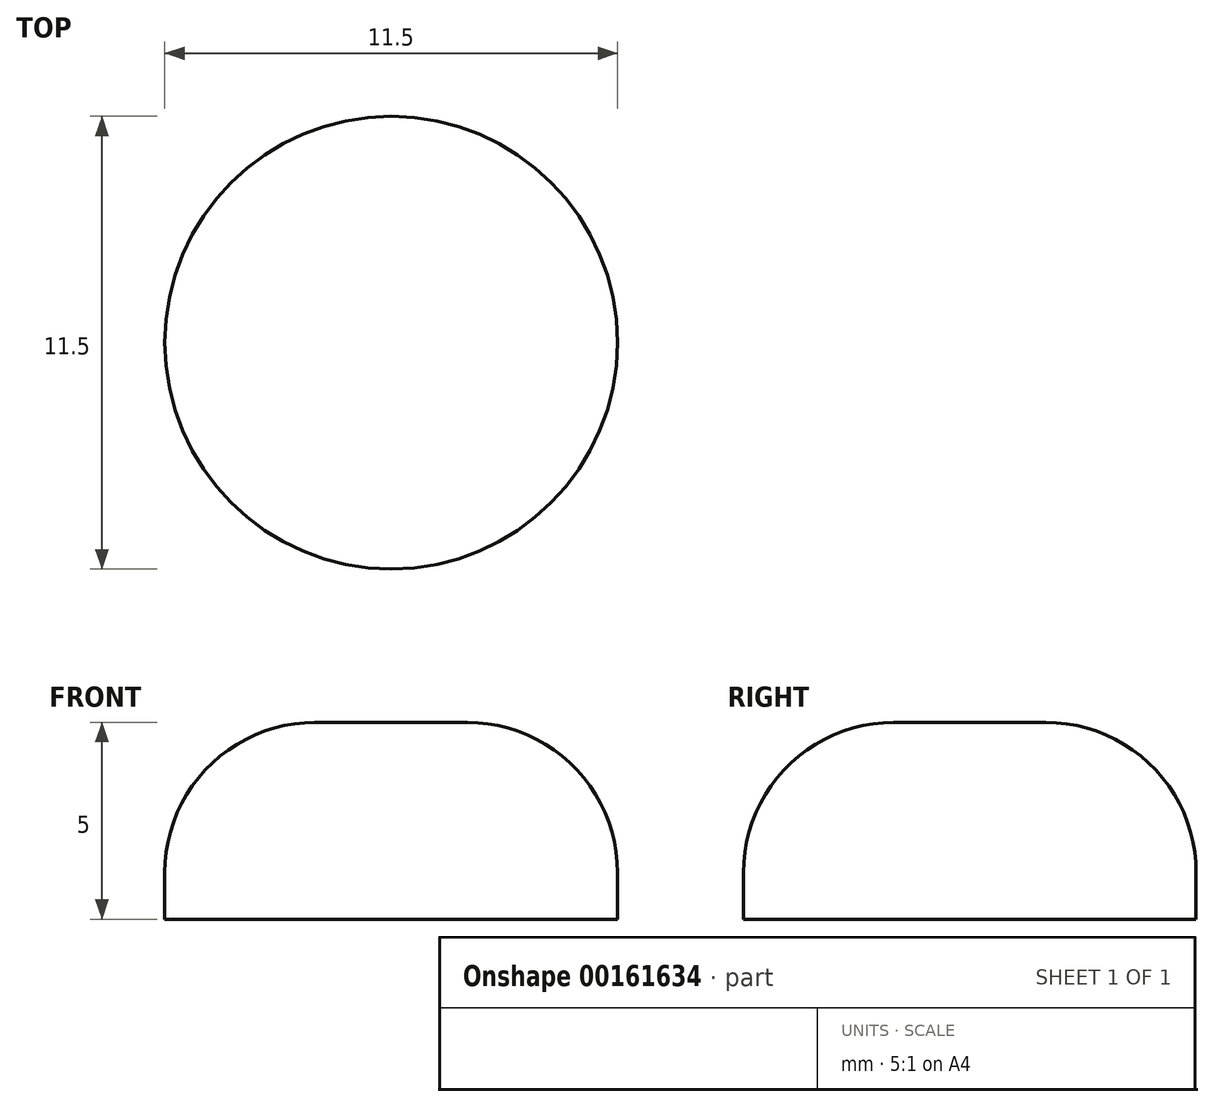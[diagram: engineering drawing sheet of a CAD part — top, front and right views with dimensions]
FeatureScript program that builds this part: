
annotation { "Feature Type Name" : "Feature", "Feature Type Description" : "" }
export const myFeature = defineFeature(function(context is Context, id is Id, definition is map)
    precondition{}
    {
        {
            var Q0;
            Q0=qCreatedBy(makeId("Top.planeOp"),FACE);
            var sketch = newSketch(context, id + "F0", { "sketchPlane" : qUnion([Q0])});
            skCircle(sketch, "E0", {"center": v(0, 0) * mm, "radius": 5.75 * mm});
            skSolve(sketch);
        }
        {
            var Q0;
            Q0 = qSketchRegion(id + "F0", true);
            extrude(context, id + "F1", {"entities" : qUnion([Q0]), "endBound" : BoundingType.SYMMETRIC, "depth" : 5 * mm});
        }
        {
            var Q0;
            Q0=makeQuery(id+"F1.opExtrude","CAP_EDGE",EDGE,{"disambiguationData":[OSD([sQuery(id+"F0.wireOp",EDGE,"E0")])],"isStart":false});
            fillet(context, id + "F2", {"entities" : qUnion([Q0]), "radius" : 3.8 * mm, "tangentPropagation" : true, "allowEdgeOverflow" : false});
        }
    });
